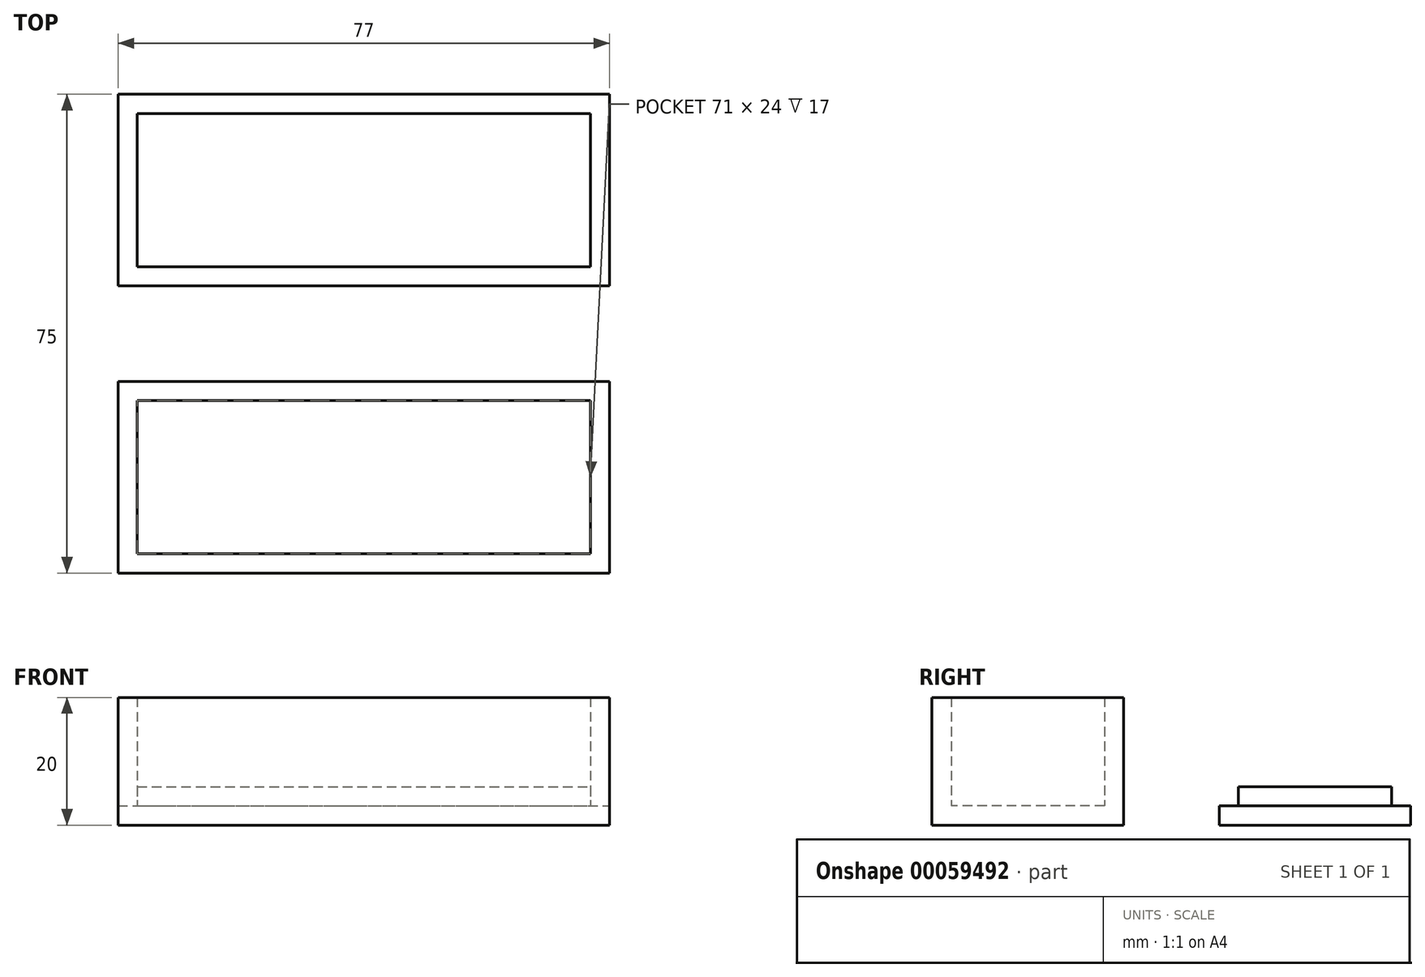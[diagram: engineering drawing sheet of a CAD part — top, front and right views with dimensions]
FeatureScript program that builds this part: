
annotation { "Feature Type Name" : "Feature", "Feature Type Description" : "" }
export const myFeature = defineFeature(function(context is Context, id is Id, definition is map)
    precondition{}
    {
        {
            var Q0;
            Q0=qCreatedBy(makeId("Top.planeOp"),FACE);
            var sketch = newSketch(context, id + "F0", { "sketchPlane" : qUnion([Q0])});
            skLineSegment(sketch, "E0.bottom", {"start": v(-38.5, 0) * mm, "end": v(38.5, 0) * mm});
            skLineSegment(sketch, "E0.top", {"start": v(-38.5, -30) * mm, "end": v(38.5, -30) * mm});
            skLineSegment(sketch, "E0.left", {"start": v(-38.5, 0) * mm, "end": v(-38.5, -30) * mm});
            skLineSegment(sketch, "E0.right", {"start": v(38.5, 0) * mm, "end": v(38.5, -30) * mm});
            skLineSegment(sketch, "E1.bottom", {"start": v(-35.5, -3) * mm, "end": v(35.5, -3) * mm});
            skLineSegment(sketch, "E1.top", {"start": v(-35.5, -27) * mm, "end": v(35.5, -27) * mm});
            skLineSegment(sketch, "E1.left", {"start": v(-35.5, -3) * mm, "end": v(-35.5, -27) * mm});
            skLineSegment(sketch, "E1.right", {"start": v(35.5, -3) * mm, "end": v(35.5, -27) * mm});
            skLineSegment(sketch, "E2", {"start": v(-38.5, -11.93) * mm, "end": v(-38.5, 49.45) * mm, "construction": true});
            skLineSegment(sketch, "E3", {"start": v(38.5, -17.14) * mm, "end": v(38.5, 50.7) * mm, "construction": true});
            skLineSegment(sketch, "E4.bottom", {"start": v(-38.5, 45) * mm, "end": v(38.5, 45) * mm});
            skLineSegment(sketch, "E4.top", {"start": v(-38.5, 15) * mm, "end": v(38.5, 15) * mm});
            skLineSegment(sketch, "E4.left", {"start": v(-38.5, 45) * mm, "end": v(-38.5, 15) * mm});
            skLineSegment(sketch, "E4.right", {"start": v(38.5, 45) * mm, "end": v(38.5, 15) * mm});
            skLineSegment(sketch, "E5.bottom", {"start": v(-35.5, 42) * mm, "end": v(35.5, 42) * mm});
            skLineSegment(sketch, "E5.top", {"start": v(-35.5, 18) * mm, "end": v(35.5, 18) * mm});
            skLineSegment(sketch, "E5.left", {"start": v(-35.5, 42) * mm, "end": v(-35.5, 18) * mm});
            skLineSegment(sketch, "E5.right", {"start": v(35.5, 42) * mm, "end": v(35.5, 18) * mm});
            skSolve(sketch);
        }
        {
            var Q0;
            Q0=makeQuery(id+"F0.imprint","IMPRINT",FACE,{"disambiguationData":[TD([[makeQuery(id+"F0.imprint","IMPRINT",EDGE,{"derivedFrom":sQuery(id+"F0.wireOp",EDGE,"E0.bottom")}),-1.0]])]});
            extrude(context, id + "F1", {"entities" : qUnion([Q0]), "depth" : 20 * mm});
        }
        {
            var Q0;
            Q0=makeQuery(id+"F0.imprint","IMPRINT",FACE,{"disambiguationData":[TD([[makeQuery(id+"F0.imprint","IMPRINT",EDGE,{"derivedFrom":sQuery(id+"F0.wireOp",EDGE,"E1.bottom")}),-1.0]])]});
            var Q1;
            Q1=makeQuery(id+"F0.imprint","IMPRINT",FACE,{"disambiguationData":[TD([[makeQuery(id+"F0.imprint","IMPRINT",EDGE,{"derivedFrom":sQuery(id+"F0.wireOp",EDGE,"E4.bottom")}),-1.0]])]});
            extrude(context, id + "F2", {"entities" : qUnion([Q0, Q1]), "operationType" : NewBodyOperationType.ADD, "depth" : 3 * mm});
        }
        {
            var Q0;
            Q0=makeQuery(id+"F0.imprint","IMPRINT",FACE,{"disambiguationData":[TD([[makeQuery(id+"F0.imprint","IMPRINT",EDGE,{"derivedFrom":sQuery(id+"F0.wireOp",EDGE,"E5.bottom")}),-1.0]])]});
            extrude(context, id + "F3", {"entities" : qUnion([Q0]), "operationType" : NewBodyOperationType.ADD, "depth" : 6 * mm});
        }
    });
